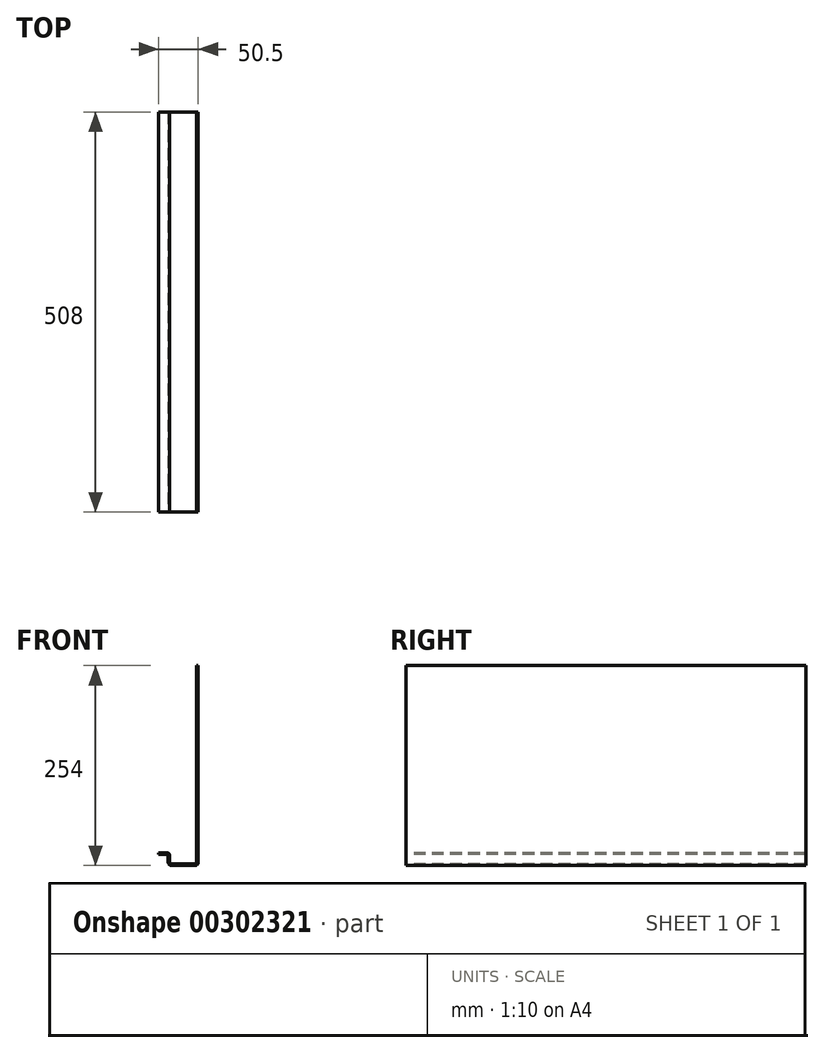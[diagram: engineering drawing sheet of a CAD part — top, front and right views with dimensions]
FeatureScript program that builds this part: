
annotation { "Feature Type Name" : "Feature", "Feature Type Description" : "" }
export const myFeature = defineFeature(function(context is Context, id is Id, definition is map)
    precondition{}
    {
        {
            var Q0;
            Q0=qCreatedBy(makeId("Front.planeOp"),FACE);
            var sketch = newSketch(context, id + "F0", { "sketchPlane" : qUnion([Q0])});
            skLineSegment(sketch, "E0", {"start": v(7.95, 7.49) * mm, "end": v(20.32, 7.49) * mm});
            skLineSegment(sketch, "E1", {"start": v(20.32, 7.49) * mm, "end": v(20.32, -6.79) * mm});
            skLineSegment(sketch, "E2", {"start": v(20.32, -6.79) * mm, "end": v(58.45, -6.79) * mm});
            skLineSegment(sketch, "E3", {"start": v(58.45, -6.79) * mm, "end": v(58.45, 247.21) * mm});
            skLineSegment(sketch, "E4", {"start": v(58.45, 247.21) * mm, "end": v(56.54, 247.21) * mm});
            skLineSegment(sketch, "E5", {"start": v(56.54, 247.21) * mm, "end": v(56.54, -4.88) * mm});
            skLineSegment(sketch, "E6", {"start": v(56.54, -4.88) * mm, "end": v(22.23, -4.88) * mm});
            skLineSegment(sketch, "E7", {"start": v(22.23, -4.88) * mm, "end": v(22.23, 9.4) * mm});
            skLineSegment(sketch, "E8", {"start": v(22.23, 9.4) * mm, "end": v(7.95, 9.4) * mm});
            skLineSegment(sketch, "E9", {"start": v(7.95, 9.4) * mm, "end": v(7.95, 7.49) * mm});
            skSolve(sketch);
        }
        {
            var Q0;
            Q0=makeQuery(id+"F0.imprint","IMPRINT",FACE,{"disambiguationData":[TD([[makeQuery(id+"F0.imprint","IMPRINT",EDGE,{"derivedFrom":sQuery(id+"F0.wireOp",EDGE,"E0")}),1.0]])]});
            extrude(context, id + "F1", {"entities" : qUnion([Q0]), "oppositeDirection" : true, "depth" : 508 * mm});
        }
        {
            var Q0;
            Q0=makeQuery(id+"F1.opExtrude","SWEPT_EDGE",EDGE,{"disambiguationData":[OSD([sQuery(id+"F0.wireOp",EDGE,"E0"),sQuery(id+"F0.wireOp",EDGE,"E1")])]});
            var Q1;
            Q1=makeQuery(id+"F1.opExtrude","SWEPT_EDGE",EDGE,{"disambiguationData":[OSD([sQuery(id+"F0.wireOp",EDGE,"E6"),sQuery(id+"F0.wireOp",EDGE,"E7")])]});
            var Q2;
            Q2=makeQuery(id+"F1.opExtrude","SWEPT_EDGE",EDGE,{"disambiguationData":[OSD([sQuery(id+"F0.wireOp",EDGE,"E5"),sQuery(id+"F0.wireOp",EDGE,"E6")])]});
            fillet(context, id + "F2", {"entities" : qUnion([Q0, Q1, Q2]), "radius" : 1.52 * mm, "tangentPropagation" : true, "allowEdgeOverflow" : false});
        }
        {
            var Q0;
            Q0=makeQuery(id+"F1.opExtrude","SWEPT_EDGE",EDGE,{"disambiguationData":[OSD([sQuery(id+"F0.wireOp",EDGE,"E7"),sQuery(id+"F0.wireOp",EDGE,"E8")])]});
            var Q1;
            Q1=makeQuery(id+"F1.opExtrude","SWEPT_EDGE",EDGE,{"disambiguationData":[OSD([sQuery(id+"F0.wireOp",EDGE,"E1"),sQuery(id+"F0.wireOp",EDGE,"E2")])]});
            var Q2;
            Q2=makeQuery(id+"F1.opExtrude","SWEPT_EDGE",EDGE,{"disambiguationData":[OSD([sQuery(id+"F0.wireOp",EDGE,"E2"),sQuery(id+"F0.wireOp",EDGE,"E3")])]});
            fillet(context, id + "F3", {"entities" : qUnion([Q0, Q1, Q2]), "radius" : 3.96 * mm, "tangentPropagation" : true, "allowEdgeOverflow" : false});
        }
    });
